# Revit family: ScanBox Duo
name_source: partatom
category: Mechanical Equipment
units: mm (PartAtom-declared; Revit-internal decimal feet)

## family parameters
Always vertical = Yes
Cut with Voids When Loaded = No
OmniClass Number = 23.75.00.00
OmniClass Title = Climate Control (HVAC)
Part Type = Normal
Room Calculation Point = No
Round Connector Dimension = Use Diameter
Shared = No
Work Plane-Based = No

## types (34) — shared parameters
Manufacturer = ScanBox Thermoproducts AB
Model = Duo
One Grip Handle = Yes
Pedal Width = 250 mm  [stored 0.82021 ft]
TapSlam Lock = No
URL = www.ScanBox.se

## per-type parameters (varying)
| type | Assembly Code | Box Depth | Box Height | Box Width | Chassi Depth | Chassi Width | Cooler 2 Compressor Left | Cooler 2 Compressor Right | Cooler Compressor Left | Cooler Compressor Right | Cooler Pelt 200 Left | Cooler Pelt 200 Right | Description | Door Swing Radius | FL Amps | Heater Single Left | Heater Single Right | Innerframe Start | Regulator 1 | Regulator 2 | TapSlam Height | Total Height | Volts |
| Ergo Line Duo HF08 + HF08 | ELDFF08 | 627 mm  [stored 2.05709 ft] | 795 mm | 980 mm  [stored 3.21522 ft] | 810 mm | 1100 mm | No | No | No | No | No | No | Ergo Line - Duo - Heating Fan - Heating Fan | 420 mm  [stored 1.37795 ft] | 6 A | Yes | Yes | 70 mm  [stored 0.229659 ft] | Yes | Yes | 248 mm  [stored 0.813648 ft] | 1074 mm | 230 V |
| Ergo Line Duo NE08 + HF08 | ELDNF08 | 627 mm  [stored 2.05709 ft] | 795 mm | 980 mm  [stored 3.21522 ft] | 810 mm | 1100 mm | No | No | No | No | No | No | Ergo Line - Duo - Neutral - Heating Fan | 420 mm  [stored 1.37795 ft] | 3 A | No | Yes | 70 mm  [stored 0.229659 ft] | Yes | No | 248 mm  [stored 0.813648 ft] | 1074 mm | 230 V |
| Ergo Line Duo CP08 + HF08 | ELDPF08 | 627 mm  [stored 2.05709 ft] | 795 mm | 980 mm  [stored 3.21522 ft] | 810 mm | 1100 mm | No | No | No | No | Yes | No | Ergo Line - Duo - Cooling Peltier - Heating Fan | 420 mm  [stored 1.37795 ft] | 5 A | No | Yes | 70 mm  [stored 0.229659 ft] | Yes | Yes | 248 mm  [stored 0.813648 ft] | 1074 mm | 230 V |
| Ergo Line Duo CC08 + HF08 | ELDCF08 | 627 mm  [stored 2.05709 ft] | 795 mm | 980 mm  [stored 3.21522 ft] | 870 mm | 1100 mm | No | No | Yes | No | No | No | Ergo Line - Duo - Cooling Compressor - Heating Fan | 420 mm  [stored 1.37795 ft] | 4 A | No | Yes | 60 mm  [stored 0.19685 ft] | Yes | Yes | 248 mm  [stored 0.813648 ft] | 1074 mm | 230 V |
| Ergo Line Duo NE08 + NE08 | ELDNN08 | 627 mm  [stored 2.05709 ft] | 795 mm | 980 mm  [stored 3.21522 ft] | 810 mm | 1100 mm | No | No | No | No | No | No | Ergo Line - Duo - Neutral - Neutral | 420 mm  [stored 1.37795 ft] | 0 A | No | No | 70 mm  [stored 0.229659 ft] | No | No | 248 mm  [stored 0.813648 ft] | 1074 mm | 0 V |
| Ergo Line Duo CP08 + CP08 | ELDPP08 | 627 mm  [stored 2.05709 ft] | 795 mm | 980 mm  [stored 3.21522 ft] | 810 mm | 1100 mm | No | No | No | No | Yes | Yes | Ergo Line - Duo - Cooling Peltier - Cooling Peltier | 420 mm  [stored 1.37795 ft] | 3 A | No | No | 70 mm  [stored 0.229659 ft] | Yes | Yes | 248 mm  [stored 0.813648 ft] | 1074 mm | 230 V |
| Ergo Line Duo CC08 + CC08 | ELDCC08 | 627 mm  [stored 2.05709 ft] | 795 mm | 980 mm  [stored 3.21522 ft] | 870 mm | 1100 mm | No | No | Yes | Yes | No | No | Ergo Line - Duo - Cooling Compressor - Cooling Compressor | 420 mm  [stored 1.37795 ft] | 2 A | No | No | 60 mm  [stored 0.19685 ft] | Yes | Yes | 248 mm  [stored 0.813648 ft] | 1074 mm | 230 V |
| Banquet Line Duo HF12 + HF12 | BLDFF12 | 752 mm | 1115 mm | 1390 mm | 910 mm | 1525 mm | No | No | No | No | No | No | Banquet Line - Duo - Heating Fan - Heating Fan | 625 mm | 16 A | Yes | Yes | 70 mm  [stored 0.229659 ft] | Yes | Yes | 320 mm | 1394 mm | 230 V |
| Banquet Line Duo CC12 + HF12 | BLDCF12 | 752 mm | 1115 mm | 1390 mm | 990 mm | 1525 mm | Yes | No | No | No | No | No | Banquet Line - Duo - Cooling Compressor - Heating Fan | 625 mm | 10 A | No | Yes | 60 mm  [stored 0.19685 ft] | Yes | Yes | 320 mm | 1394 mm | 230 V |
| Banquet Line Duo CC12 + CC12 | BLDCC12 | 752 mm | 1115 mm | 1390 mm | 990 mm | 1525 mm | Yes | Yes | No | No | No | No | Banquet Line - Duo - Cooling Compressor - Cooling Compressor | 625 mm | 3 A | No | No | 60 mm  [stored 0.19685 ft] | Yes | Yes | 320 mm | 1394 mm | 230 V |
| Ergo Line Duo NE12 + NE12 | ELDNN12 | 627 mm  [stored 2.05709 ft] | 1115 mm | 980 mm  [stored 3.21522 ft] | 810 mm | 1100 mm | No | No | No | No | No | No | Ergo Line - Duo - Neutral - Neutral | 420 mm  [stored 1.37795 ft] | 0 A | No | No | 70 mm  [stored 0.229659 ft] | No | No | 320 mm | 1394 mm | 0 V |
| Ergo Line Duo NE14 + NE14 | ELDNN14 | 627 mm  [stored 2.05709 ft] | 1275 mm | 980 mm  [stored 3.21522 ft] | 810 mm | 1100 mm | No | No | No | No | No | No | Ergo Line - Duo - Neutral - Neutral | 420 mm  [stored 1.37795 ft] | 0 A | No | No | 70 mm  [stored 0.229659 ft] | No | No | 480 mm | 1554 mm | 0 V |
| Ergo Line Duo HF12 + HF12 | ELDFF12 | 627 mm  [stored 2.05709 ft] | 1115 mm | 980 mm  [stored 3.21522 ft] | 810 mm | 1100 mm | No | No | No | No | No | No | Ergo Line - Duo - Heating Fan - Heating Fan | 420 mm  [stored 1.37795 ft] | 9 A | Yes | Yes | 70 mm  [stored 0.229659 ft] | Yes | Yes | 320 mm | 1394 mm | 230 V |
| Ergo Line Duo HF14 + HF14 | ELDFF14 | 627 mm  [stored 2.05709 ft] | 1275 mm | 980 mm  [stored 3.21522 ft] | 810 mm | 1100 mm | No | No | No | No | No | No | Ergo Line - Duo - Heating Fan - Heating Fan | 420 mm  [stored 1.37795 ft] | 9 A | Yes | Yes | 70 mm  [stored 0.229659 ft] | Yes | Yes | 480 mm | 1554 mm | 230 V |
| Ergo Line Duo CP12 + CP12 | ELDPP12 | 627 mm  [stored 2.05709 ft] | 1115 mm | 980 mm  [stored 3.21522 ft] | 810 mm | 1100 mm | No | No | No | No | Yes | Yes | Ergo Line - Duo - Cooling Peltier - Cooling Peltier | 420 mm  [stored 1.37795 ft] | 3 A | No | No | 70 mm  [stored 0.229659 ft] | Yes | Yes | 320 mm | 1394 mm | 230 V |
| Ergo Line Duo CP14 + CP14 | ELDPP14 | 627 mm  [stored 2.05709 ft] | 1275 mm | 980 mm  [stored 3.21522 ft] | 810 mm | 1100 mm | No | No | No | No | Yes | Yes | Ergo Line - Duo - Cooling Peltier - Cooling Peltier | 420 mm  [stored 1.37795 ft] | 3 A | No | No | 70 mm  [stored 0.229659 ft] | Yes | Yes | 480 mm | 1554 mm | 230 V |
| Ergo Line Duo CC12 + CC12 | ELDCC12 | 627 mm  [stored 2.05709 ft] | 1115 mm | 980 mm  [stored 3.21522 ft] | 870 mm | 1100 mm | No | No | Yes | Yes | No | No | Ergo Line - Duo - Cooling Compressor - Cooling Compressor | 420 mm  [stored 1.37795 ft] | 2 A | No | No | 60 mm  [stored 0.19685 ft] | Yes | Yes | 320 mm | 1394 mm | 230 V |
| Ergo Line Duo CC14 + CC14 | ELDCC14 | 627 mm  [stored 2.05709 ft] | 1275 mm | 980 mm  [stored 3.21522 ft] | 870 mm | 1100 mm | No | No | Yes | Yes | No | No | Ergo Line - Duo - Cooling Compressor - Cooling Compressor | 420 mm  [stored 1.37795 ft] | 2 A | No | No | 60 mm  [stored 0.19685 ft] | Yes | Yes | 480 mm | 1554 mm | 230 V |
| Ergo Line Duo NE12 + HF12 | ELDNF12 | 627 mm  [stored 2.05709 ft] | 1115 mm | 980 mm  [stored 3.21522 ft] | 810 mm | 1100 mm | No | No | No | No | No | No | Ergo Line - Duo - Neutral - Heating Fan | 420 mm  [stored 1.37795 ft] | 5 A | No | Yes | 70 mm  [stored 0.229659 ft] | Yes | No | 320 mm | 1394 mm | 230 V |
| Ergo Line Duo NE14 + HF14 | ELDNF14 | 627 mm  [stored 2.05709 ft] | 1275 mm | 980 mm  [stored 3.21522 ft] | 810 mm | 1100 mm | No | No | No | No | No | No | Ergo Line - Duo - Neutral - Heating Fan | 420 mm  [stored 1.37795 ft] | 5 A | No | Yes | 70 mm  [stored 0.229659 ft] | Yes | No | 480 mm | 1554 mm | 230 V |
| Ergo Line Duo CP12 + HF12 | ELDPF12 | 627 mm  [stored 2.05709 ft] | 1115 mm | 980 mm  [stored 3.21522 ft] | 810 mm | 1100 mm | No | No | No | No | Yes | No | Ergo Line - Duo - Cooling Peltier - Heating Fan | 420 mm  [stored 1.37795 ft] | 6 A | No | Yes | 70 mm  [stored 0.229659 ft] | Yes | Yes | 320 mm | 1394 mm | 230 V |
| Ergo Line Duo CP14 + HF14 | ELDPF14 | 627 mm  [stored 2.05709 ft] | 1275 mm | 980 mm  [stored 3.21522 ft] | 810 mm | 1100 mm | No | No | No | No | Yes | No | Ergo Line - Duo - Cooling Peltier - Heating Fan | 420 mm  [stored 1.37795 ft] | 6 A | No | Yes | 70 mm  [stored 0.229659 ft] | Yes | Yes | 480 mm | 1554 mm | 230 V |
| Ergo Line Duo CC12 + HF12 | ELDCF12 | 627 mm  [stored 2.05709 ft] | 1115 mm | 980 mm  [stored 3.21522 ft] | 870 mm | 1100 mm | No | No | Yes | No | No | No | Ergo Line - Duo - Cooling Compressor - Heating Fan | 420 mm  [stored 1.37795 ft] | 5 A | No | Yes | 60 mm  [stored 0.19685 ft] | Yes | Yes | 320 mm | 1394 mm | 230 V |
| Ergo Line Duo CC14 + HF14 | ELDCF14 | 627 mm  [stored 2.05709 ft] | 1275 mm | 980 mm  [stored 3.21522 ft] | 870 mm | 1100 mm | No | No | Yes | No | No | No | Ergo Line - Duo - Cooling Compressor - Heating Fan | 420 mm  [stored 1.37795 ft] | 5 A | No | Yes | 60 mm  [stored 0.19685 ft] | Yes | Yes | 480 mm | 1554 mm | 230 V |
| Banquet Line Duo HF16 + HF16 | BLDFF16 | 752 mm | 1435 mm | 1390 mm | 910 mm | 1525 mm | No | No | No | No | No | No | Banquet Line - Duo - Heating Fan - Heating Fan | 625 mm | 16 A | Yes | Yes | 70 mm  [stored 0.229659 ft] | Yes | Yes | 640 mm | 1714 mm | 230 V |
| Banquet Line Duo CC16 + CC16 | BLDCC16 | 752 mm | 1435 mm | 1390 mm | 990 mm | 1525 mm | Yes | Yes | No | No | No | No | Banquet Line - Duo - Cooling Compressor - Cooling Compressor | 625 mm | 3 A | No | No | 60 mm  [stored 0.19685 ft] | Yes | Yes | 640 mm | 1714 mm | 230 V |
| Banquet Line Duo CC16 + HF16 | BLDCF16 | 752 mm | 1435 mm | 1390 mm | 990 mm | 1525 mm | Yes | No | No | No | No | No | Banquet Line - Duo - Cooling Compressor - Heating Fan | 625 mm | 10 A | No | Yes | 60 mm  [stored 0.19685 ft] | Yes | Yes | 640 mm | 1714 mm | 230 V |
| Ergo Line Duo NE10 + NE10 | ELDNN10 | 627 mm  [stored 2.05709 ft] | 955 mm  [stored 3.1332 ft] | 980 mm  [stored 3.21522 ft] | 810 mm | 1100 mm | No | No | No | No | No | No | Ergo Line - Duo - Neutral - Neutral | 420 mm  [stored 1.37795 ft] | 0 A | No | No | 70 mm  [stored 0.229659 ft] | No | No | 480 mm | 1234 mm  [stored 4.04856 ft] | 0 V |
| Ergo Line Duo HF10 + HF10 | ELDFF10 | 627 mm  [stored 2.05709 ft] | 955 mm  [stored 3.1332 ft] | 980 mm  [stored 3.21522 ft] | 810 mm | 1100 mm | No | No | No | No | No | No | Ergo Line - Duo - Heating Fan - Heating Fan | 420 mm  [stored 1.37795 ft] | 6 A | Yes | Yes | 70 mm  [stored 0.229659 ft] | Yes | Yes | 320 mm | 1234 mm  [stored 4.04856 ft] | 230 V |
| Ergo Line Duo CP10 + CP10 | ELDPP10 | 627 mm  [stored 2.05709 ft] | 955 mm  [stored 3.1332 ft] | 980 mm  [stored 3.21522 ft] | 810 mm | 1100 mm | No | No | No | No | Yes | Yes | Ergo Line - Duo - Cooling Peltier - Cooling Peltier | 420 mm  [stored 1.37795 ft] | 3 A | No | No | 70 mm  [stored 0.229659 ft] | Yes | Yes | 248 mm  [stored 0.813648 ft] | 1234 mm  [stored 4.04856 ft] | 230 V |
| Ergo Line Duo CC10 + CC10 | ELDCC10 | 627 mm  [stored 2.05709 ft] | 955 mm  [stored 3.1332 ft] | 980 mm  [stored 3.21522 ft] | 870 mm | 1100 mm | No | No | Yes | Yes | No | No | Ergo Line - Duo - Cooling Compressor - Cooling Compressor | 420 mm  [stored 1.37795 ft] | 2 A | No | No | 60 mm  [stored 0.19685 ft] | Yes | Yes | 248 mm  [stored 0.813648 ft] | 1234 mm  [stored 4.04856 ft] | 230 V |
| Ergo Line Duo NE10 + HF10 | ELDNF10 | 627 mm  [stored 2.05709 ft] | 955 mm  [stored 3.1332 ft] | 980 mm  [stored 3.21522 ft] | 810 mm | 1100 mm | No | No | No | No | No | No | Ergo Line - Duo - Neutral - Heating Fan | 420 mm  [stored 1.37795 ft] | 3 A | No | Yes | 70 mm  [stored 0.229659 ft] | Yes | No | 248 mm  [stored 0.813648 ft] | 1234 mm  [stored 4.04856 ft] | 230 V |
| Ergo Line Duo CP10 + HF10 | ELDPF10 | 627 mm  [stored 2.05709 ft] | 955 mm  [stored 3.1332 ft] | 980 mm  [stored 3.21522 ft] | 810 mm | 1100 mm | No | No | No | No | Yes | No | Ergo Line - Duo - Cooling Peltier - Heating Fan | 420 mm  [stored 1.37795 ft] | 5 A | No | Yes | 70 mm  [stored 0.229659 ft] | Yes | Yes | 248 mm  [stored 0.813648 ft] | 1234 mm  [stored 4.04856 ft] | 230 V |
| Ergo Line Duo CC10 + HF10 | ELDCF10 | 627 mm  [stored 2.05709 ft] | 955 mm  [stored 3.1332 ft] | 980 mm  [stored 3.21522 ft] | 870 mm | 1100 mm | No | No | Yes | No | No | No | Ergo Line - Duo - Cooling Compressor - Heating Fan | 420 mm  [stored 1.37795 ft] | 4 A | No | Yes | 60 mm  [stored 0.19685 ft] | Yes | Yes | 248 mm  [stored 0.813648 ft] | 1234 mm  [stored 4.04856 ft] | 230 V |

note: [stored X ft] marks values corroborated as IEEE doubles in the binary element streams (Revit-internal decimal feet)

## geometry (parser evidence)
native form markers: Sweep x7
no freeform markers — native parametric forms only
